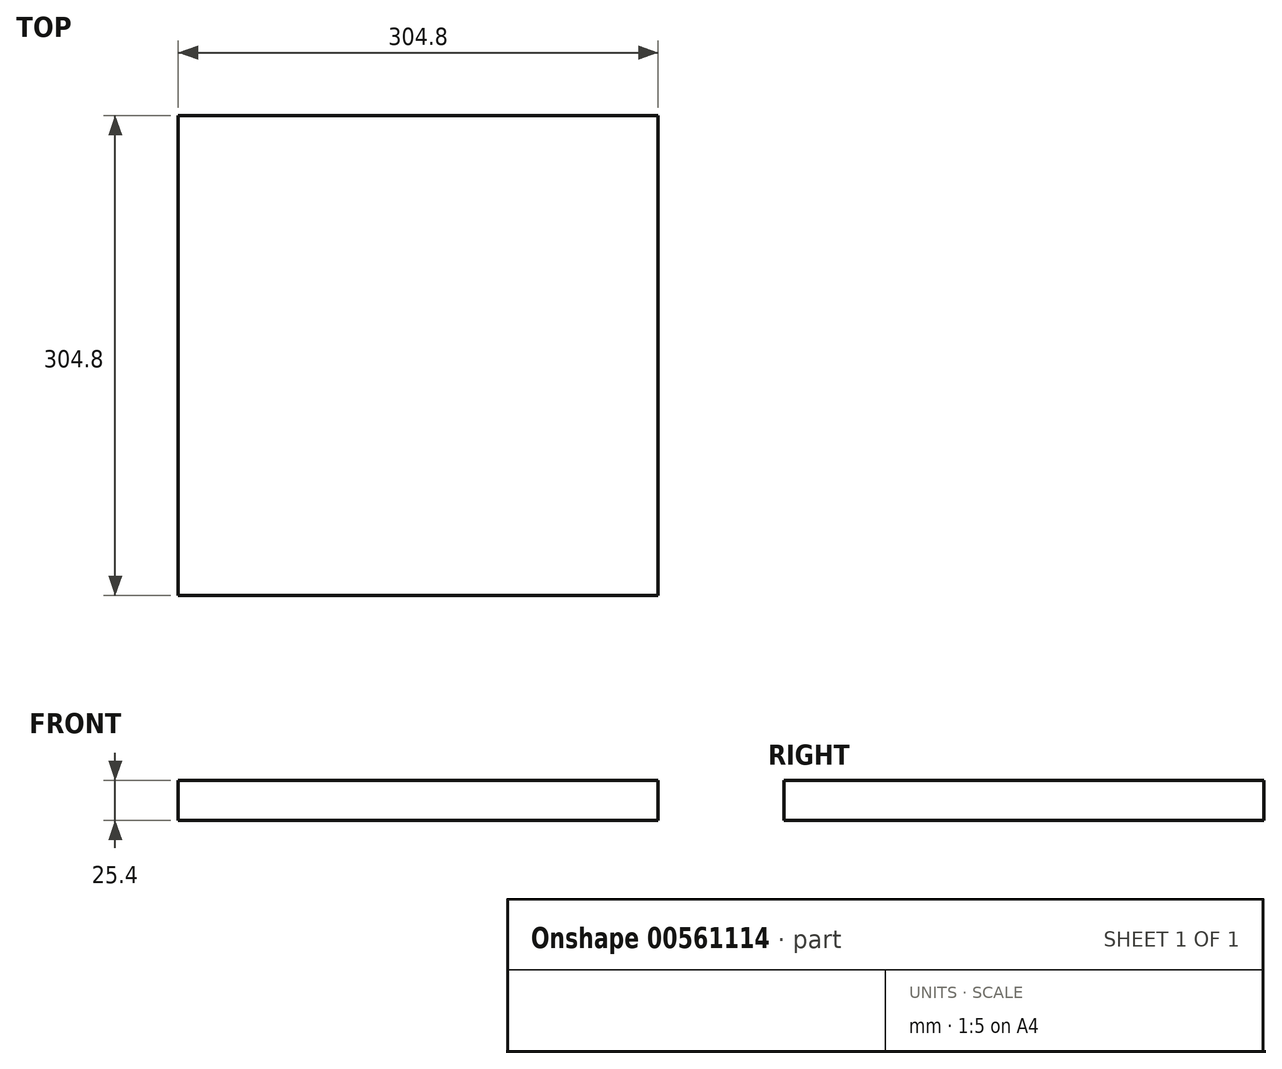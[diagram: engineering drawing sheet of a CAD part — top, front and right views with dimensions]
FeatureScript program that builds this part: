
annotation { "Feature Type Name" : "Feature", "Feature Type Description" : "" }
export const myFeature = defineFeature(function(context is Context, id is Id, definition is map)
    precondition{}
    {
        {
            var Q0;
            Q0=qCreatedBy(makeId("Top.planeOp"),FACE);
            var sketch = newSketch(context, id + "F0", { "sketchPlane" : qUnion([Q0])});
            skLineSegment(sketch, "E0.bottom", {"start": v(0, 0) * mm, "end": v(304.8, 0) * mm});
            skLineSegment(sketch, "E0.top", {"start": v(0, 304.8) * mm, "end": v(304.8, 304.8) * mm});
            skLineSegment(sketch, "E0.left", {"start": v(0, 0) * mm, "end": v(0, 304.8) * mm});
            skLineSegment(sketch, "E0.right", {"start": v(304.8, 0) * mm, "end": v(304.8, 304.8) * mm});
            skSolve(sketch);
        }
        {
            var Q0;
            Q0=makeQuery(id+"F0.imprint","IMPRINT",FACE,{"disambiguationData":[TD([[makeQuery(id+"F0.imprint","IMPRINT",EDGE,{"derivedFrom":sQuery(id+"F0.wireOp",EDGE,"E0.bottom")}),1.0]])]});
            extrude(context, id + "F1", {"entities" : qUnion([Q0]), "depth" : 25.4 * mm, "offsetDistance" : 25.4 * mm});
        }
    });
